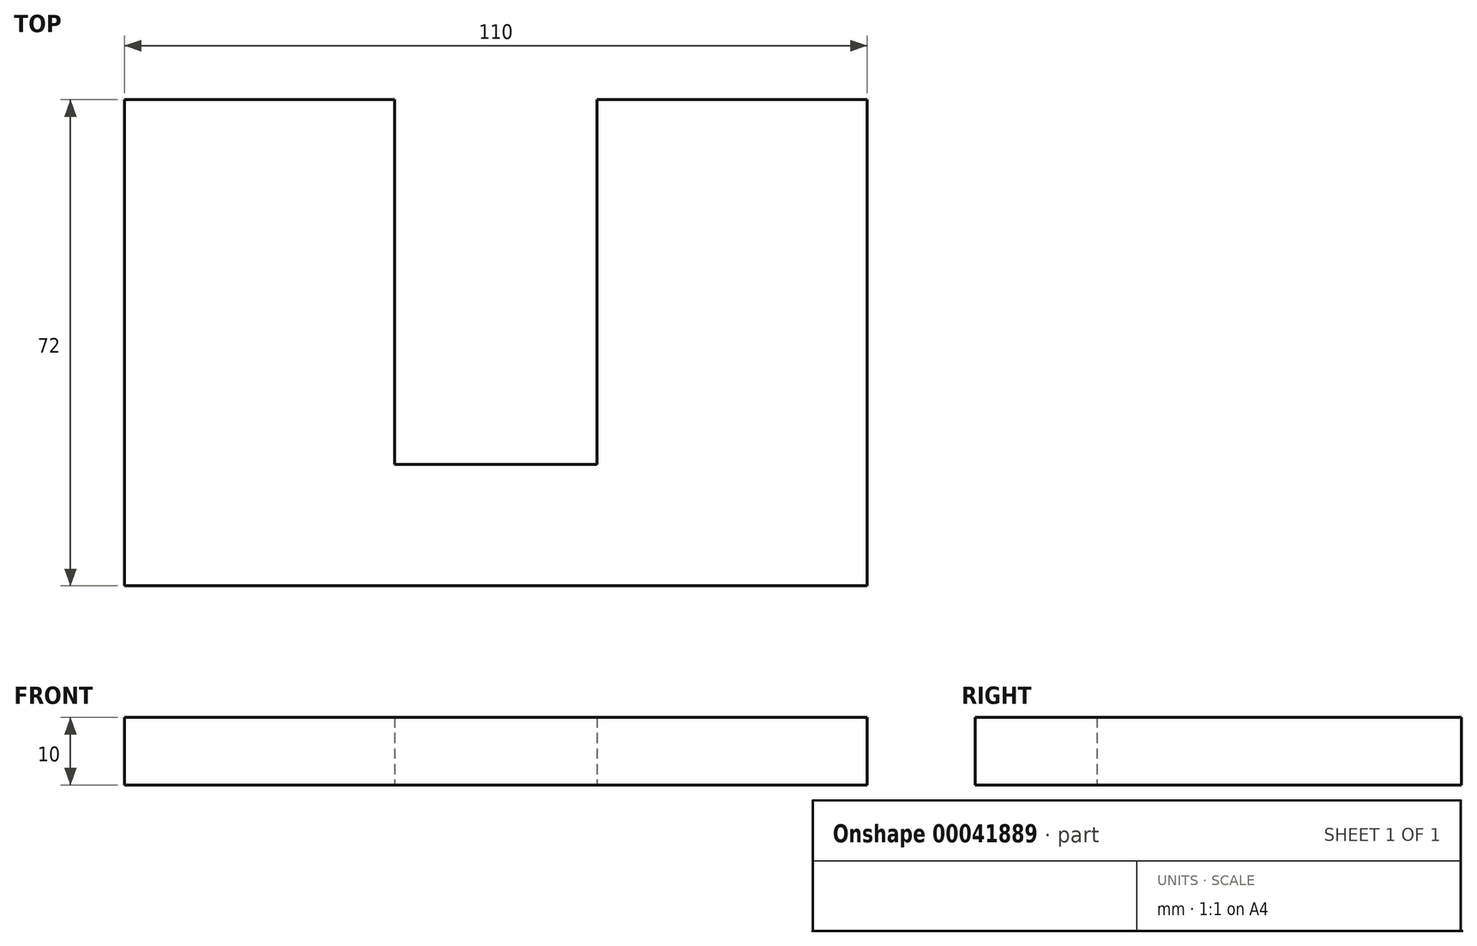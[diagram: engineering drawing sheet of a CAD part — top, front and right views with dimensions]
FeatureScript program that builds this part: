
annotation { "Feature Type Name" : "Feature", "Feature Type Description" : "" }
export const myFeature = defineFeature(function(context is Context, id is Id, definition is map)
    precondition{}
    {
        {
            var Q0;
            Q0=qCreatedBy(makeId("Top.planeOp"),FACE);
            var sketch = newSketch(context, id + "F0", { "sketchPlane" : qUnion([Q0])});
            skLineSegment(sketch, "E0.bottom", {"start": v(-75.35, 53.57) * mm, "end": v(-35.35, 53.57) * mm});
            skLineSegment(sketch, "E0.top", {"start": v(-75.35, -18.43) * mm, "end": v(-35.35, -18.43) * mm});
            skLineSegment(sketch, "E0.left", {"start": v(-75.35, 53.57) * mm, "end": v(-75.35, -18.43) * mm});
            skLineSegment(sketch, "E0.right", {"start": v(-35.35, 53.57) * mm, "end": v(-35.35, -18.43) * mm});
            skLineSegment(sketch, "E1.bottom", {"start": v(-35.35, -0.43) * mm, "end": v(-5.35, -0.43) * mm});
            skLineSegment(sketch, "E1.top", {"start": v(-35.35, -18.43) * mm, "end": v(-5.35, -18.43) * mm});
            skLineSegment(sketch, "E1.left", {"start": v(-35.35, -0.43) * mm, "end": v(-35.35, -18.43) * mm});
            skLineSegment(sketch, "E1.right", {"start": v(-5.35, -0.43) * mm, "end": v(-5.35, -18.43) * mm});
            skLineSegment(sketch, "E2.bottom", {"start": v(-5.35, 53.57) * mm, "end": v(34.65, 53.57) * mm});
            skLineSegment(sketch, "E2.top", {"start": v(-5.35, -18.43) * mm, "end": v(34.65, -18.43) * mm});
            skLineSegment(sketch, "E2.left", {"start": v(-5.35, 53.57) * mm, "end": v(-5.35, -18.43) * mm});
            skLineSegment(sketch, "E2.right", {"start": v(34.65, 53.57) * mm, "end": v(34.65, -18.43) * mm});
            skSolve(sketch);
        }
        {
            var Q0;
            Q0=makeQuery(id+"F0.imprint","IMPRINT",FACE,{"disambiguationData":[TD([[makeQuery(id+"F0.imprint","IMPRINT",EDGE,{"derivedFrom":sQuery(id+"F0.wireOp",EDGE,"E0.bottom")}),-1.0]])]});
            var Q1;
            {var subQ2=sQuery(id+"F0.wireOp",EDGE,"E1.bottom");Q1=makeQuery(id+"F0.imprint","IMPRINT",FACE,{"disambiguationData":[TD([[makeQuery(id+"F0.imprint","IMPRINT",EDGE,{"derivedFrom":subQ2}),-1.0]])]});}
            var Q2;
            {var subQ0=sQuery(id+"F0.wireOp",EDGE,"E2.bottom");Q2=makeQuery(id+"F0.imprint","IMPRINT",FACE,{"disambiguationData":[TD([[makeQuery(id+"F0.imprint","IMPRINT",EDGE,{"derivedFrom":subQ0}),-1.0]])]});}
            extrude(context, id + "F1", {"entities" : qUnion([Q0, Q1, Q2]), "depth" : 10 * mm});
        }
    });
